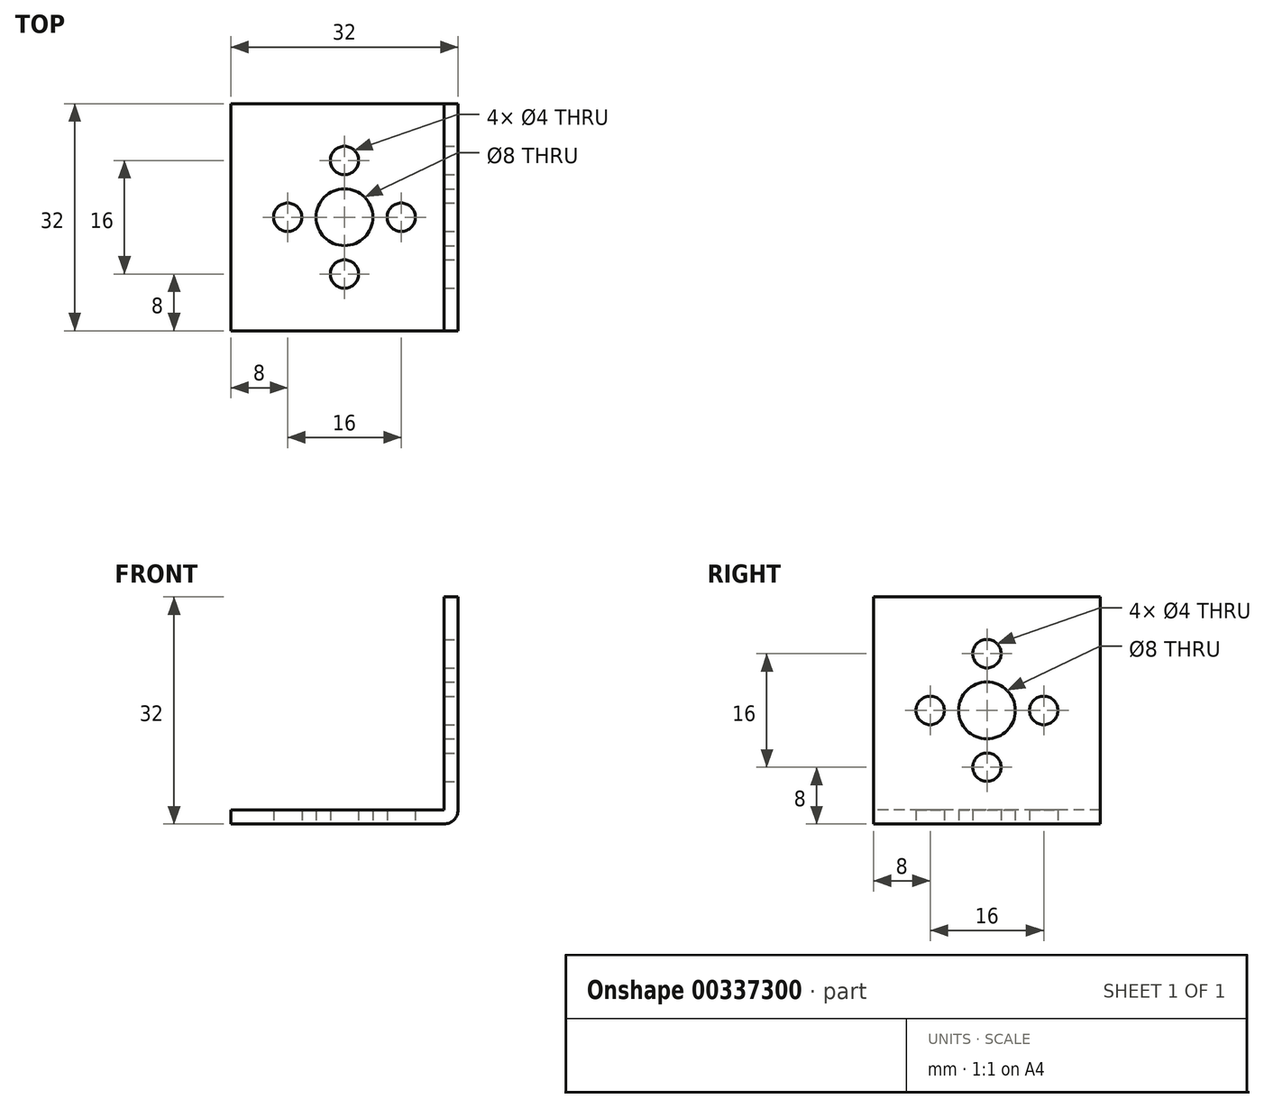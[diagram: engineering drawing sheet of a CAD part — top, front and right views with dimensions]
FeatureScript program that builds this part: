
annotation { "Feature Type Name" : "Feature", "Feature Type Description" : "" }
export const myFeature = defineFeature(function(context is Context, id is Id, definition is map)
    precondition{}
    {
        {
            var Q0;
            Q0=qCreatedBy(makeId("Top.planeOp"),FACE);
            var sketch = newSketch(context, id + "F0", { "sketchPlane" : qUnion([Q0])});
            skLineSegment(sketch, "E0.bottom", {"start": v(16, 16) * mm, "end": v(-16, 16) * mm});
            skLineSegment(sketch, "E0.top", {"start": v(16, -16) * mm, "end": v(-16, -16) * mm});
            skLineSegment(sketch, "E0.left", {"start": v(16, 16) * mm, "end": v(16, -16) * mm});
            skLineSegment(sketch, "E0.right", {"start": v(-16, 16) * mm, "end": v(-16, -16) * mm});
            skPoint(sketch, "E0.middle", {"position": v(0, 0) * mm});
            skCircle(sketch, "E1", {"center": v(0, 0) * mm, "radius": 4 * mm});
            skCircle(sketch, "E2", {"center": v(0, 8) * mm, "radius": 2 * mm});
            skCircle(sketch, "E3", {"center": v(8, 0) * mm, "radius": 2 * mm});
            skCircle(sketch, "E4", {"center": v(0, -8) * mm, "radius": 2 * mm});
            skCircle(sketch, "E5", {"center": v(-8, 0) * mm, "radius": 2 * mm});
            skSolve(sketch);
        }
        {
            var Q0;
            Q0=sQuery(id+"F0.wireOp",EDGE,"E0.left");
            var Q1;
            Q1=qCreatedBy(makeId("Right.planeOp"),FACE);
            cPlane(context, id + "F1", {"entities" : qUnion([Q0, Q1]), "cplaneType" : CPlaneType.LINE_ANGLE, "offset" : 25.4 * mm, "angle" : 0 * degree, "width" : 152.4 * mm, "height" : 152.4 * mm});
        }
        {
            var Q0;
            Q0=qCreatedBy(id+"F1.planeOp",FACE);
            var sketch = newSketch(context, id + "F2", { "sketchPlane" : qUnion([Q0])});
            skLineSegment(sketch, "E6.bottom", {"start": v(16, 0) * mm, "end": v(-16, 0) * mm});
            skLineSegment(sketch, "E6.top", {"start": v(16, 32) * mm, "end": v(-16, 32) * mm});
            skLineSegment(sketch, "E6.left", {"start": v(16, 0) * mm, "end": v(16, 32) * mm});
            skLineSegment(sketch, "E6.right", {"start": v(-16, 0) * mm, "end": v(-16, 32) * mm});
            skPoint(sketch, "E7.middle", {"position": v(0, 16) * mm});
            skCircle(sketch, "E8", {"center": v(0, 16) * mm, "radius": 4 * mm});
            skCircle(sketch, "E9", {"center": v(0, 24) * mm, "radius": 2 * mm});
            skCircle(sketch, "E10", {"center": v(8, 16) * mm, "radius": 2 * mm});
            skCircle(sketch, "E11", {"center": v(0, 8) * mm, "radius": 2 * mm});
            skCircle(sketch, "E12", {"center": v(-8, 16) * mm, "radius": 2 * mm});
            skPoint(sketch, "E13", {"position": v(16, 16) * mm});
            skSolve(sketch);
        }
        {
            var Q0;
            Q0=makeQuery(id+"F0.imprint","IMPRINT",FACE,{"disambiguationData":[TD([[makeQuery(id+"F0.imprint","IMPRINT",EDGE,{"derivedFrom":sQuery(id+"F0.wireOp",EDGE,"E0.bottom")}),1.0]])]});
            extrude(context, id + "F3", {"entities" : qUnion([Q0]), "depth" : 2 * mm});
        }
        {
            var Q0;
            Q0=makeQuery(id+"F2.imprint","IMPRINT",FACE,{"disambiguationData":[TD([[makeQuery(id+"F2.imprint","IMPRINT",EDGE,{"derivedFrom":sQuery(id+"F2.wireOp",EDGE,"E6.bottom")}),-1.0]])]});
            extrude(context, id + "F4", {"entities" : qUnion([Q0]), "operationType" : NewBodyOperationType.ADD, "depth" : 2 * mm});
        }
        {
            var Q0;
            Q0=makeQuery(id+"F3.opExtrude","CAP_EDGE",EDGE,{"disambiguationData":[OSD([sQuery(id+"F0.wireOp",EDGE,"E0.left")])],"isStart":true});
            fillet(context, id + "F5", {"entities" : qUnion([Q0]), "radius" : 2 * mm, "tangentPropagation" : true, "allowEdgeOverflow" : false});
        }
    });
